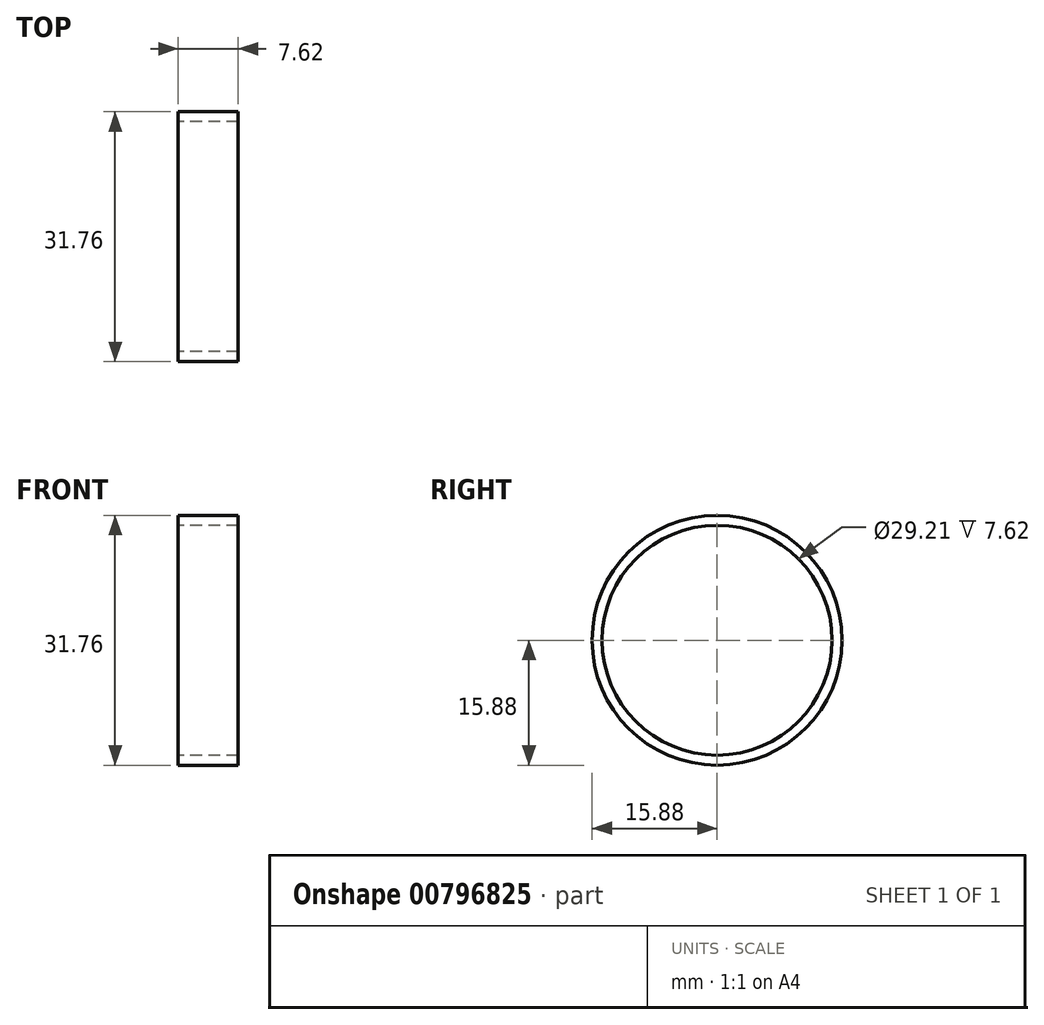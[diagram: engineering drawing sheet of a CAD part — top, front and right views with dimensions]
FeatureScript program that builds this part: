
annotation { "Feature Type Name" : "Feature", "Feature Type Description" : "" }
export const myFeature = defineFeature(function(context is Context, id is Id, definition is map)
    precondition{}
    {
        {
            var Q0;
            Q0=qCreatedBy(makeId("Right.planeOp"),FACE);
            var sketch = newSketch(context, id + "F0", { "sketchPlane" : qUnion([Q0])});
            skLineSegment(sketch, "E0", {"start": v(0, 0) * mm, "end": v(0, 21.59) * mm});
            skCircle(sketch, "E1", {"center": v(0, 21.59) * mm, "radius": 14.6 * mm});
            skCircle(sketch, "E2", {"center": v(0, 21.59) * mm, "radius": 15.88 * mm});
            skSolve(sketch);
        }
        {
            var Q0;
            Q0=makeQuery(id+"F0.imprint","IMPRINT",FACE,{"disambiguationData":[TD([[makeQuery(id+"F0.imprint","IMPRINT",EDGE,{"derivedFrom":sQuery(id+"F0.wireOp",EDGE,"E1")}),-1.0]])]});
            extrude(context, id + "F1", {"entities" : qUnion([Q0]), "depth" : 7.62 * mm, "offsetDistance" : 25.4 * mm});
        }
    });
